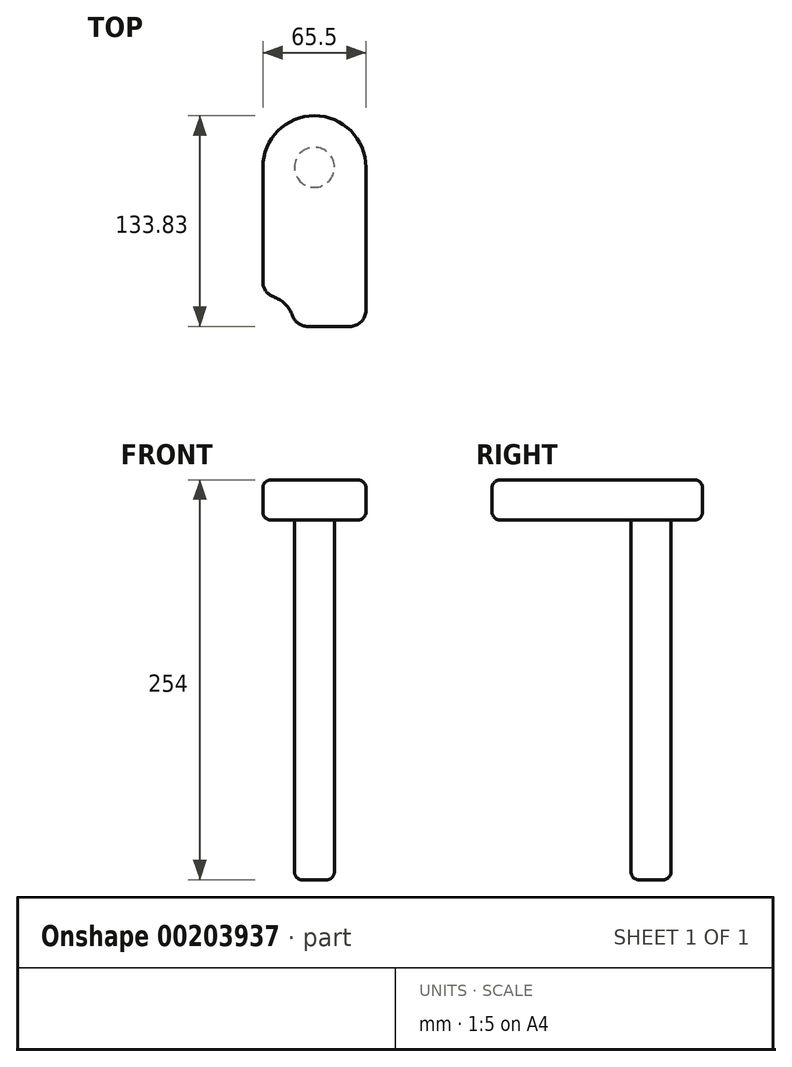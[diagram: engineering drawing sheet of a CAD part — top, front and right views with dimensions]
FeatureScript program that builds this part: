
annotation { "Feature Type Name" : "Feature", "Feature Type Description" : "" }
export const myFeature = defineFeature(function(context is Context, id is Id, definition is map)
    precondition{}
    {
        {
            var Q0;
            Q0=qCreatedBy(makeId("Top.planeOp"),FACE);
            var sketch = newSketch(context, id + "F0", { "sketchPlane" : qUnion([Q0])});
            skArc(sketch, "E0", {"start": v(26.5, 118.1) * mm, "mid": v(-6.26, 150.85) * mm, "end": v(-39.01, 118.1) * mm});
            skLineSegment(sketch, "E1", {"start": v(-39.01, 118.1) * mm, "end": v(-39.01, 37.07) * mm});
            skLineSegment(sketch, "E2", {"start": v(26.5, 118.1) * mm, "end": v(26.5, 17.02) * mm});
            skLineSegment(sketch, "E3", {"start": v(26.5, 17.02) * mm, "end": v(-18.96, 17.02) * mm});
            skCircle(sketch, "E4", {"center": v(-6.26, 118.1) * mm, "radius": 12.7 * mm});
            skArc(sketch, "E5", {"start": v(-18.96, 17.02) * mm, "mid": v(-24.83, 31.2) * mm, "end": v(-39.01, 37.07) * mm});
            skSolve(sketch);
        }
        {
            var Q0;
            Q0=makeQuery(id+"F0.imprint","IMPRINT",FACE,{"disambiguationData":[TD([[makeQuery(id+"F0.imprint","IMPRINT",EDGE,{"derivedFrom":sQuery(id+"F0.wireOp",EDGE,"E0")}),1.0]])]});
            extrude(context, id + "F1", {"entities" : qUnion([Q0]), "depth" : 25.4 * mm});
        }
        {
            var Q0;
            Q0=makeQuery(id+"F1.opExtrude","CAP_FACE",FACE,{"disambiguationData":[OSD([sQuery(id+"F0.wireOp",EDGE,"E0"),sQuery(id+"F0.wireOp",EDGE,"E1"),sQuery(id+"F0.wireOp",EDGE,"E2"),sQuery(id+"F0.wireOp",EDGE,"E3"),sQuery(id+"F0.wireOp",EDGE,"dn1uQKJz-HALG-QJ90-ZuTS-B6Vmyy9tqG1u"),sQuery(id+"F0.wireOp",EDGE,"E4")])],"isStart":false});
            var sketch = newSketch(context, id + "F2", { "sketchPlane" : qUnion([Q0])});
            skCircle(sketch, "E6", {"center": v(-6.26, 118.1) * mm, "radius": 12.7 * mm});
            skSolve(sketch);
        }
        {
            var Q0;
            Q0=makeQuery(id+"F2.imprint","IMPRINT",FACE,{"disambiguationData":[TD([[makeQuery(id+"F2.imprint","IMPRINT",EDGE,{"derivedFrom":sQuery(id+"F2.wireOp",EDGE,"E6")}),1.0]])]});
            extrude(context, id + "F3", {"entities" : qUnion([Q0]), "operationType" : NewBodyOperationType.ADD, "oppositeDirection" : true, "depth" : 254 * mm});
        }
        {
            var Q0;
            Q0=makeQuery(id+"F3.opExtrude","CAP_EDGE",EDGE,{"disambiguationData":[OSD([sQuery(id+"F2.wireOp",EDGE,"E6")])],"isStart":false});
            fillet(context, id + "F4", {"entities" : qUnion([Q0]), "radius" : 5.08 * mm, "tangentPropagation" : true, "allowEdgeOverflow" : false});
        }
        {
            var Q0;
            Q0=makeQuery(id+"F1.opExtrude","SWEPT_EDGE",EDGE,{"disambiguationData":[OSD([sQuery(id+"F0.wireOp",EDGE,"E2"),sQuery(id+"F0.wireOp",EDGE,"E3")])]});
            var Q1;
            Q1=makeQuery(id+"F1.opExtrude","SWEPT_EDGE",EDGE,{"disambiguationData":[OSD([sQuery(id+"F0.wireOp",EDGE,"E3"),sQuery(id+"F0.wireOp",EDGE,"E5")])]});
            var Q2;
            Q2=makeQuery(id+"F1.opExtrude","SWEPT_EDGE",EDGE,{"disambiguationData":[OSD([sQuery(id+"F0.wireOp",EDGE,"E1"),sQuery(id+"F0.wireOp",EDGE,"E5")])]});
            fillet(context, id + "F5", {"entities" : qUnion([Q0, Q1, Q2]), "radius" : 10.16 * mm, "tangentPropagation" : true, "allowEdgeOverflow" : false});
        }
        {
            var Q0;
            Q0=makeQuery(id+"F1.opExtrude","CAP_EDGE",EDGE,{"disambiguationData":[OSD([sQuery(id+"F0.wireOp",EDGE,"E1")])],"isStart":false});
            var Q1;
            Q1=makeQuery(id+"F1.opExtrude","CAP_EDGE",EDGE,{"disambiguationData":[OSD([sQuery(id+"F0.wireOp",EDGE,"E1")])],"isStart":true});
            fillet(context, id + "F6", {"entities" : qUnion([Q0, Q1]), "radius" : 5.08 * mm, "tangentPropagation" : true, "allowEdgeOverflow" : false});
        }
    });
